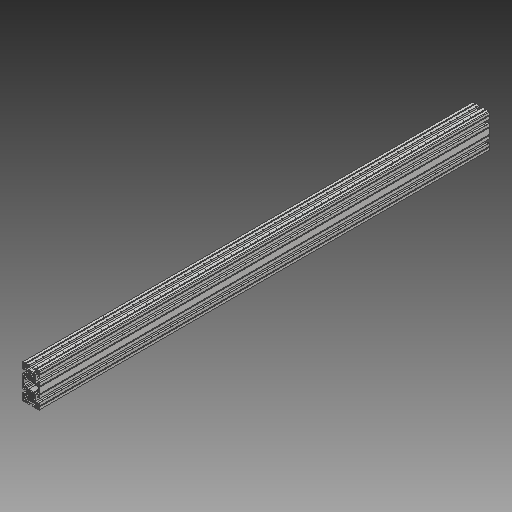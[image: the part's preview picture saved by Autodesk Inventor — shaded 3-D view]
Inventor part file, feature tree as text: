
AUTODESK INVENTOR PART (.ipt)
format: ipt  version: 2018 (Build 220112000, 112)  size: 640,512 bytes
history: native  units: mm
features: other x1, extrude x1, sketch x1
ambient origin geometry x8: Origin, YZ Plane, XZ Plane, XY Plane, X Axis, Y Axis, Z Axis, Center Point
bodies: Body1 (feature_tree)
feature tree (3):
  other  "Sólido1"
  extrude  "Extrusão1"  [1 undecoded]
  sketch  "Esboço1"  dims[d0=1054.0mm d1=0.0mm]
note: 1 required parameter value undecoded (feature->parameter linkage not recoverable at this tier; creation-order binding heuristic only, values carry confidence <= 0.55)
